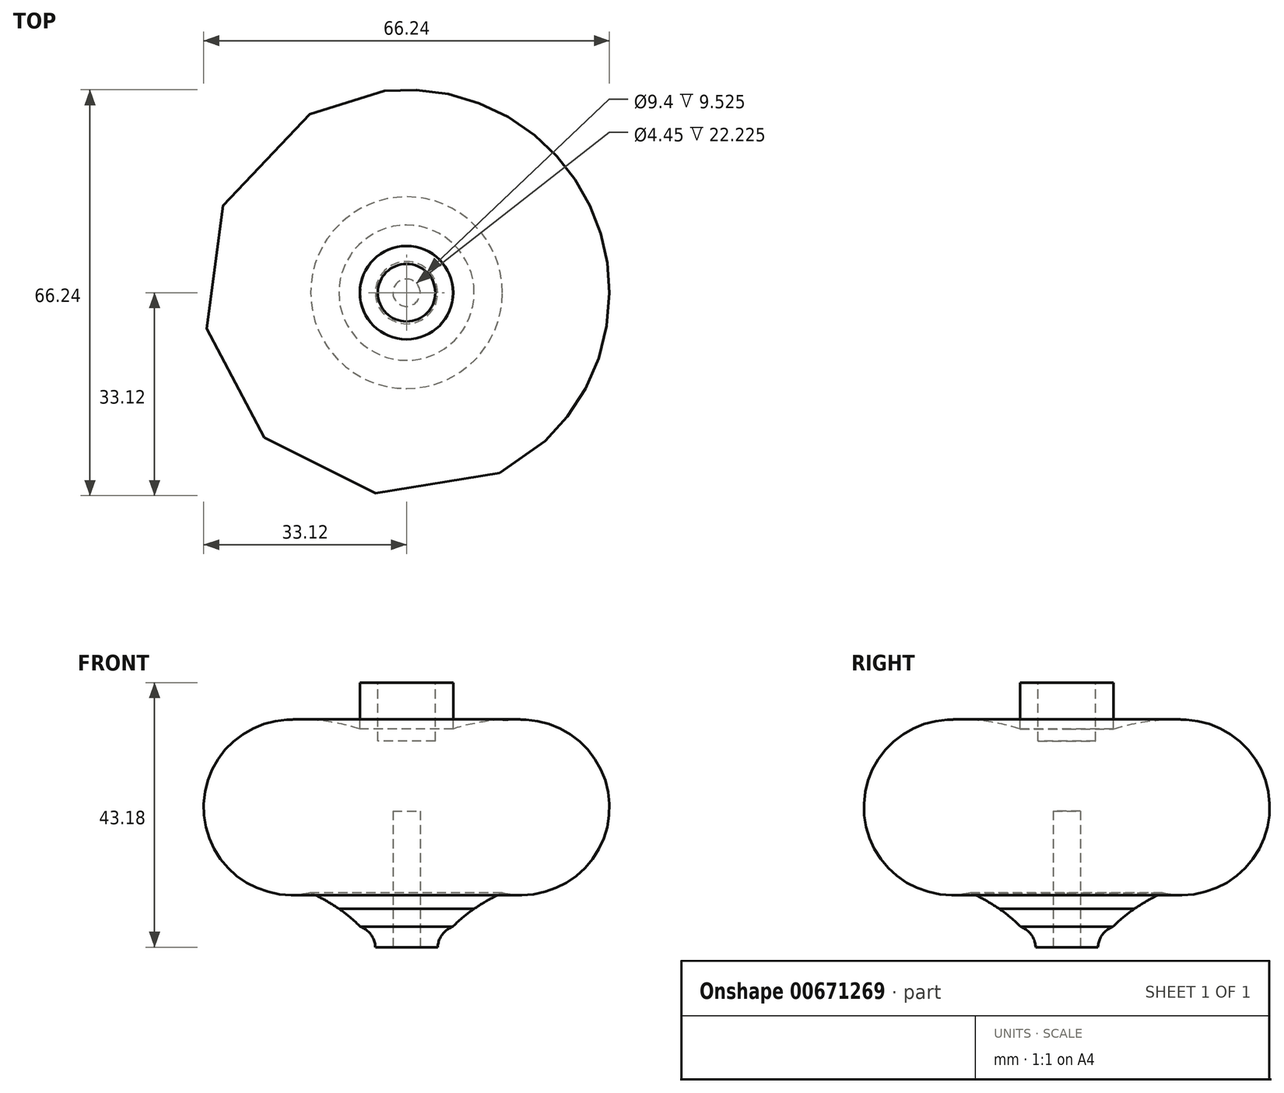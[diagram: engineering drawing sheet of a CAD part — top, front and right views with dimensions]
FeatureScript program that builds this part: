
annotation { "Feature Type Name" : "Feature", "Feature Type Description" : "" }
export const myFeature = defineFeature(function(context is Context, id is Id, definition is map)
    precondition{}
    {
        {
            var Q0;
            Q0=qCreatedBy(makeId("Front.planeOp"),FACE);
            var sketch = newSketch(context, id + "F0", { "sketchPlane" : qUnion([Q0])});
            skArc(sketch, "E0", {"start": v(15.64, -79.3) * mm, "mid": v(33, -67.28) * mm, "end": v(19.51, -51.05) * mm});
            skLineSegment(sketch, "E1", {"start": v(7.62, -52.53) * mm, "end": v(7.62, -44.98) * mm});
            skLineSegment(sketch, "E2", {"start": v(7.62, -44.98) * mm, "end": v(0, -44.98) * mm});
            skLineSegment(sketch, "E3", {"start": v(0, -44.98) * mm, "end": v(0, -88.16) * mm});
            skArc(sketch, "E4", {"start": v(15.64, -79.3) * mm, "mid": v(13.29, -80.5) * mm, "end": v(11.03, -81.9) * mm});
            skLineSegment(sketch, "E5", {"start": v(5.08, -88.16) * mm, "end": v(0, -88.16) * mm});
            skPoint(sketch, "E6", {"position": v(31.75, -59.22) * mm});
            skArc(sketch, "E7", {"start": v(7.51, -84.84) * mm, "mid": v(5.8, -86.14) * mm, "end": v(5.08, -88.16) * mm});
            skArc(sketch, "E8", {"start": v(11.03, -81.9) * mm, "mid": v(9.2, -83.29) * mm, "end": v(7.51, -84.84) * mm});
            skArc(sketch, "E9", {"start": v(19.51, -51.05) * mm, "mid": v(13.5, -51.25) * mm, "end": v(7.62, -52.53) * mm});
            skSolve(sketch);
        }
        {
            var Q0;
            Q0 = qSketchRegion(id + "F0", true);
            var Q1;
            Q1=sQuery(id+"F0.wireOp",EDGE,"E3");
            revolve(context, id + "F1", {"entities" : qUnion([Q0]), "axis" : qUnion([Q1]), "revolveType" : RevolveType.FULL});
        }
        {
            var Q0;
            Q0=makeQuery(id+"F1.opRevolve","SWEPT_FACE",FACE,{"disambiguationData":[OSD([sQuery(id+"F0.wireOp",EDGE,"E2")])]});
            var sketch = newSketch(context, id + "F2", { "sketchPlane" : qUnion([Q0])});
            skCircle(sketch, "E10", {"center": v(0, 0) * mm, "radius": 4.7 * mm});
            skSolve(sketch);
        }
        {
            var Q0;
            Q0 = qSketchRegion(id + "F2", true);
            var Q1;
            Q1 = qSketchRegion(id + "F4", true);
            extrude(context, id + "F3", {"entities" : qUnion([Q0, Q1]), "operationType" : NewBodyOperationType.REMOVE, "oppositeDirection" : true, "depth" : 9.52 * mm, "offsetDistance" : 25.4 * mm});
        }
        {
            var Q0;
            Q0=makeQuery(id+"F1.opRevolve","SWEPT_FACE",FACE,{"disambiguationData":[OSD([sQuery(id+"F0.wireOp",EDGE,"E5")])]});
            var sketch = newSketch(context, id + "F4", { "sketchPlane" : qUnion([Q0])});
            skCircle(sketch, "E11", {"center": v(0, 0) * mm, "radius": 2.22 * mm});
            skSolve(sketch);
        }
        {
            var Q0;
            Q0 = qSketchRegion(id + "F4", true);
            var Q1;
            Q1=makeQuery(id+"F1.opRevolve","SWEPT_FACE",FACE,{"disambiguationData":[OSD([sQuery(id+"F0.wireOp",EDGE,"E2")])]});
            extrude(context, id + "F5", {"entities" : qUnion([Q0, Q1]), "operationType" : NewBodyOperationType.REMOVE, "oppositeDirection" : true, "depth" : 22.22 * mm, "offsetDistance" : 25.4 * mm});
        }
    });
